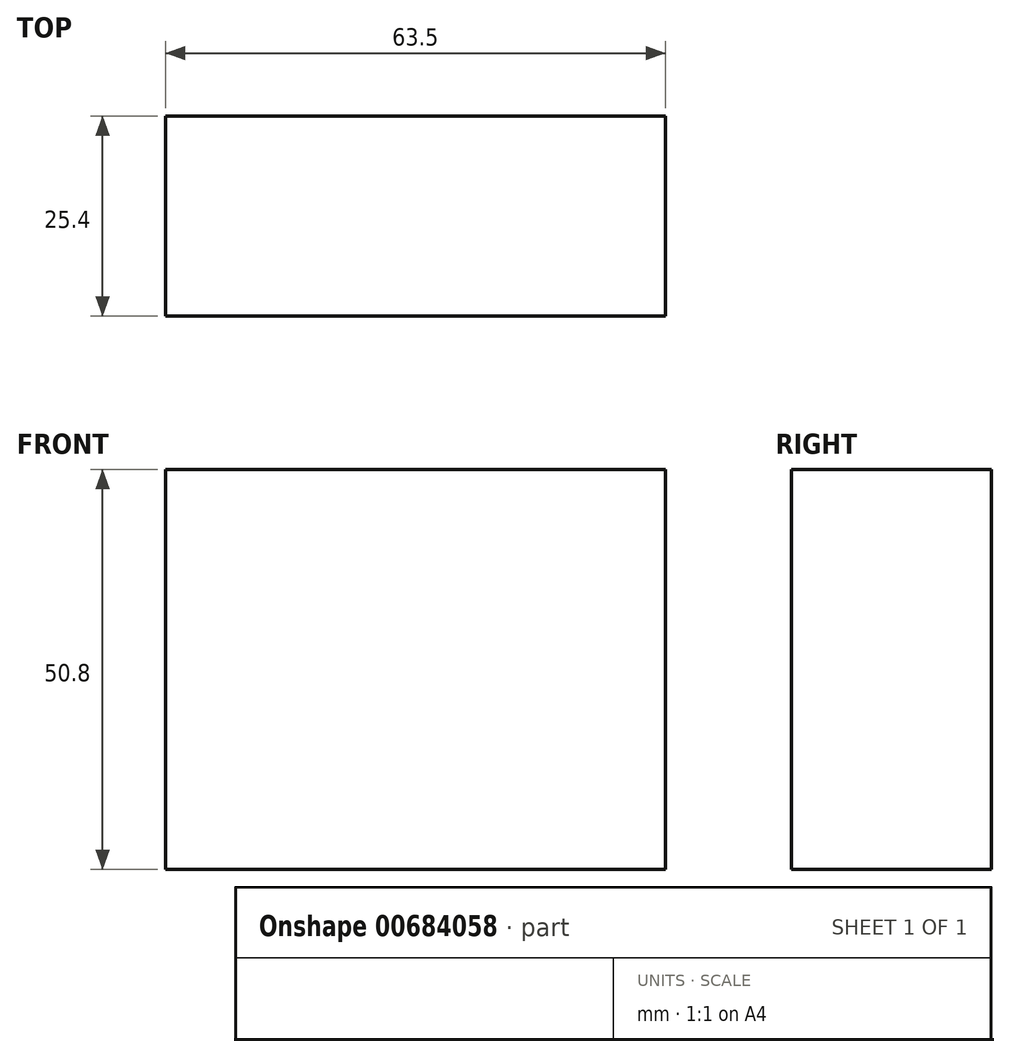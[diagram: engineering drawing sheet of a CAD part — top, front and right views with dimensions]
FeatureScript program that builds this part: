
annotation { "Feature Type Name" : "Feature", "Feature Type Description" : "" }
export const myFeature = defineFeature(function(context is Context, id is Id, definition is map)
    precondition{}
    {
        {
            var Q0;
            Q0=qCreatedBy(makeId("Front.planeOp"),FACE);
            var sketch = newSketch(context, id + "F0", { "sketchPlane" : qUnion([Q0])});
            skLineSegment(sketch, "E0.bottom", {"start": v(31.75, 25.4) * mm, "end": v(-31.75, 25.4) * mm});
            skLineSegment(sketch, "E0.top", {"start": v(31.75, -25.4) * mm, "end": v(-31.75, -25.4) * mm});
            skLineSegment(sketch, "E0.left", {"start": v(31.75, 25.4) * mm, "end": v(31.75, -25.4) * mm});
            skLineSegment(sketch, "E0.right", {"start": v(-31.75, 25.4) * mm, "end": v(-31.75, -25.4) * mm});
            skPoint(sketch, "E0.middle", {"position": v(0, 0) * mm});
            skSolve(sketch);
        }
        {
            var Q0;
            Q0=makeQuery(id+"F0.imprint","IMPRINT",FACE,{"disambiguationData":[TD([[makeQuery(id+"F0.imprint","IMPRINT",EDGE,{"derivedFrom":sQuery(id+"F0.wireOp",EDGE,"E0.bottom")}),1.0]])]});
            extrude(context, id + "F1", {"entities" : qUnion([Q0]), "endBound" : BoundingType.SYMMETRIC, "depth" : 25.4 * mm, "offsetDistance" : 25.4 * mm});
        }
    });
